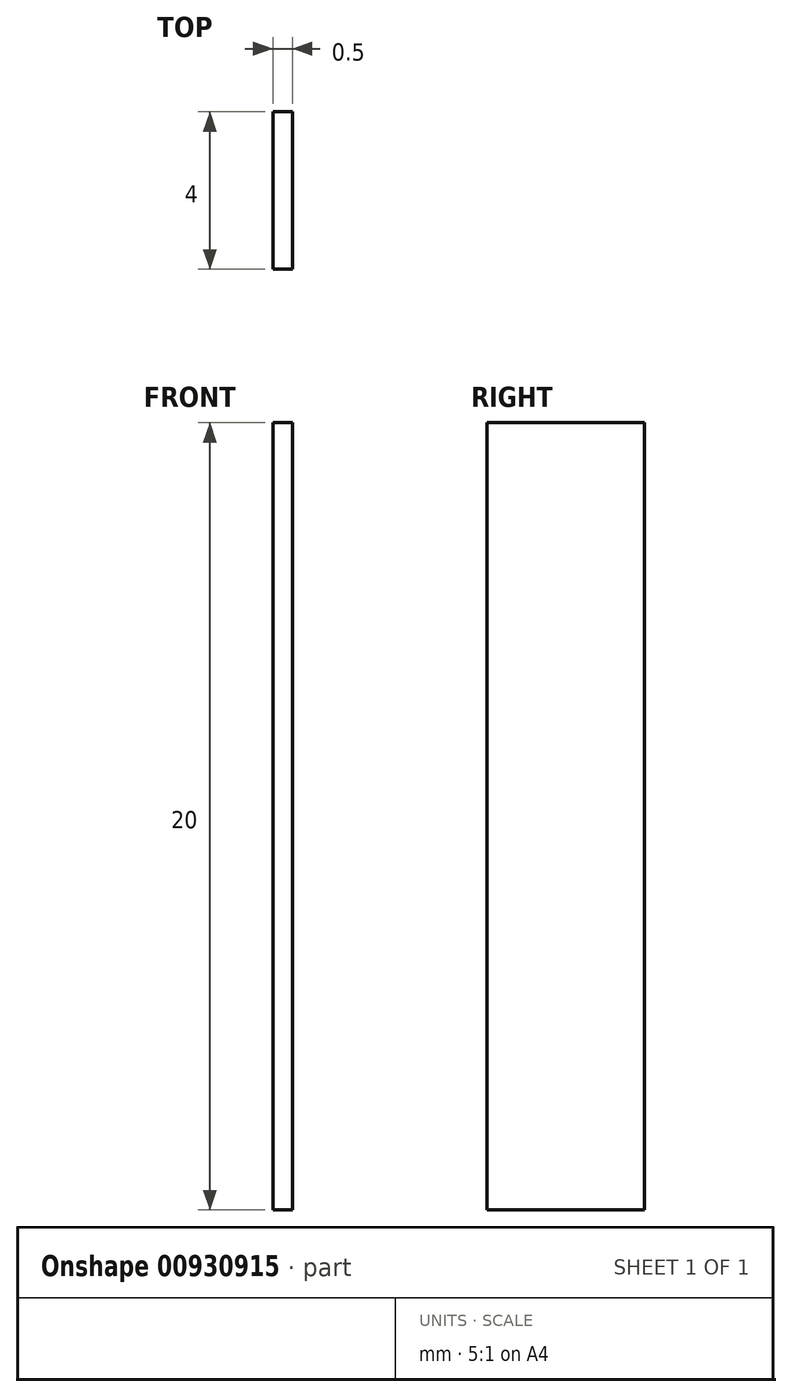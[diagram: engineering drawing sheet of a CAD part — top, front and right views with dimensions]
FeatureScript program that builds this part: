
annotation { "Feature Type Name" : "Feature", "Feature Type Description" : "" }
export const myFeature = defineFeature(function(context is Context, id is Id, definition is map)
    precondition{}
    {
        {
            var Q0;
            Q0=qCreatedBy(makeId("Right.planeOp"),FACE);
            var sketch = newSketch(context, id + "F0", { "sketchPlane" : qUnion([Q0])});
            skLineSegment(sketch, "E0.bottom", {"start": v(2, 10) * mm, "end": v(-2, 10) * mm});
            skLineSegment(sketch, "E0.top", {"start": v(2, -10) * mm, "end": v(-2, -10) * mm});
            skLineSegment(sketch, "E0.left", {"start": v(2, 10) * mm, "end": v(2, -10) * mm});
            skLineSegment(sketch, "E0.right", {"start": v(-2, 10) * mm, "end": v(-2, -10) * mm});
            skPoint(sketch, "E0.middle", {"position": v(0, 0) * mm});
            skSolve(sketch);
        }
        {
            var Q0;
            Q0=makeQuery(id+"F0.imprint","IMPRINT",FACE,{"disambiguationData":[TD([[makeQuery(id+"F0.imprint","IMPRINT",EDGE,{"derivedFrom":sQuery(id+"F0.wireOp",EDGE,"E0.bottom")}),1.0]])]});
            extrude(context, id + "F1", {"entities" : qUnion([Q0]), "depth" : 0.5 * mm, "offsetDistance" : 25 * mm});
        }
    });
